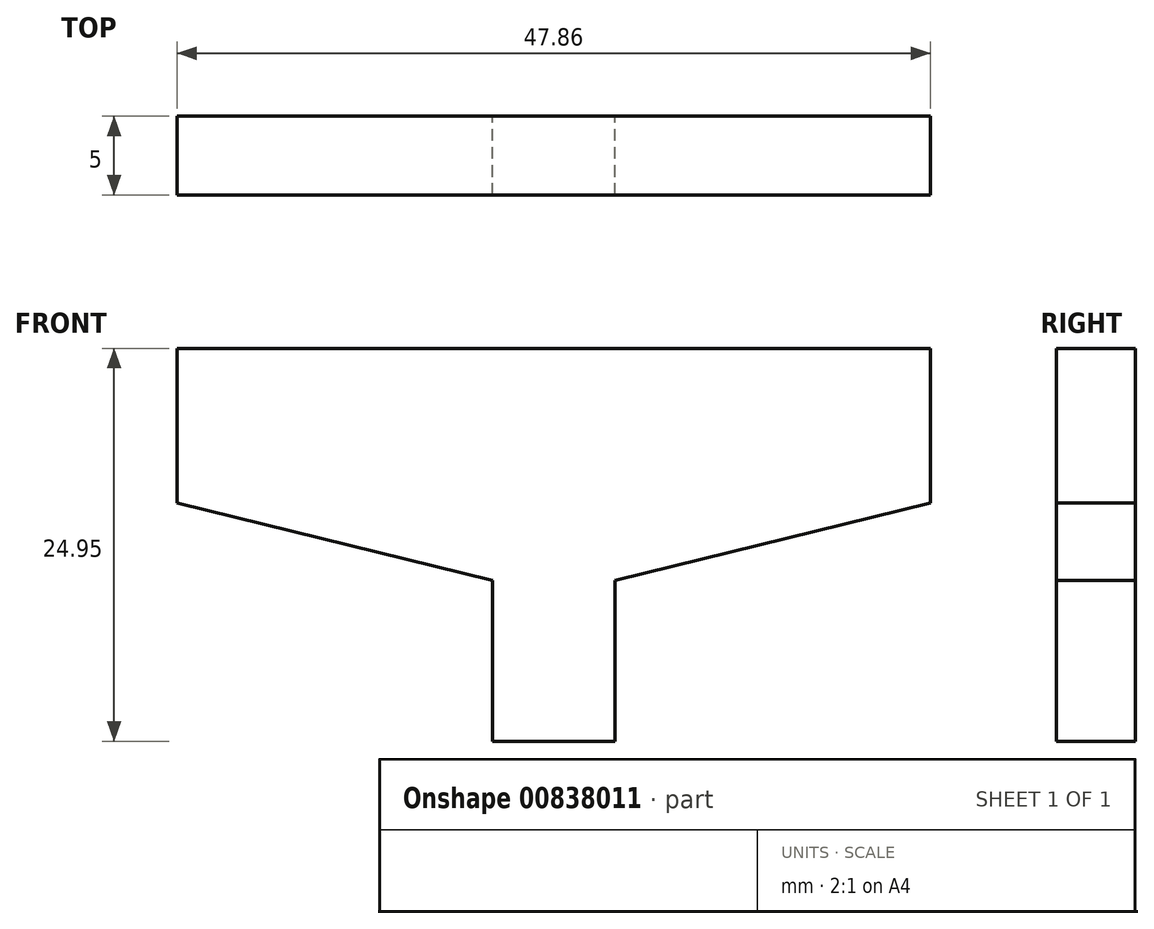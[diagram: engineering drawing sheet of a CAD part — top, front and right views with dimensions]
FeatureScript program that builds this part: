
annotation { "Feature Type Name" : "Feature", "Feature Type Description" : "" }
export const myFeature = defineFeature(function(context is Context, id is Id, definition is map)
    precondition{}
    {
        {
            var Q0;
            Q0=qCreatedBy(makeId("Front.planeOp"),FACE);
            var sketch = newSketch(context, id + "F0", { "sketchPlane" : qUnion([Q0])});
            skLineSegment(sketch, "E0", {"start": v(0, -18.82) * mm, "end": v(-3.89, -18.82) * mm});
            skLineSegment(sketch, "E1", {"start": v(-3.89, -18.82) * mm, "end": v(-3.89, -8.6) * mm});
            skLineSegment(sketch, "E2", {"start": v(-3.89, -8.6) * mm, "end": v(-23.93, -3.68) * mm});
            skLineSegment(sketch, "E3", {"start": v(-23.93, -3.68) * mm, "end": v(-23.93, 6.13) * mm});
            skLineSegment(sketch, "E4", {"start": v(-23.93, 6.13) * mm, "end": v(0, 6.13) * mm});
            skLineSegment(sketch, "E5", {"start": v(0, 6.13) * mm, "end": v(0, -18.82) * mm});
            skSolve(sketch);
        }
        {
            var Q0;
            Q0 = qSketchRegion(id + "F0", true);
            extrude(context, id + "F1", {"entities" : qUnion([Q0]), "depth" : 5 * mm, "offsetDistance" : 25 * mm});
        }
        {
            var Q0;
            Q0=makeQuery(id+"F1.opExtrude","SWEPT_BODY",BODY,{"disambiguationData":[OSD([sQuery(id+"F0.wireOp",EDGE,"E0"),sQuery(id+"F0.wireOp",EDGE,"E1"),sQuery(id+"F0.wireOp",EDGE,"E2"),sQuery(id+"F0.wireOp",EDGE,"E3"),sQuery(id+"F0.wireOp",EDGE,"E4"),sQuery(id+"F0.wireOp",EDGE,"E5")])]});
            var Q1;
            Q1=qCreatedBy(makeId("Right.planeOp"),FACE);
            mirror(context, id + "F2", {"operationType" : NewBodyOperationType.ADD, "entities" : qUnion([Q0]), "mirrorPlane" : qUnion([Q1])});
        }
    });
